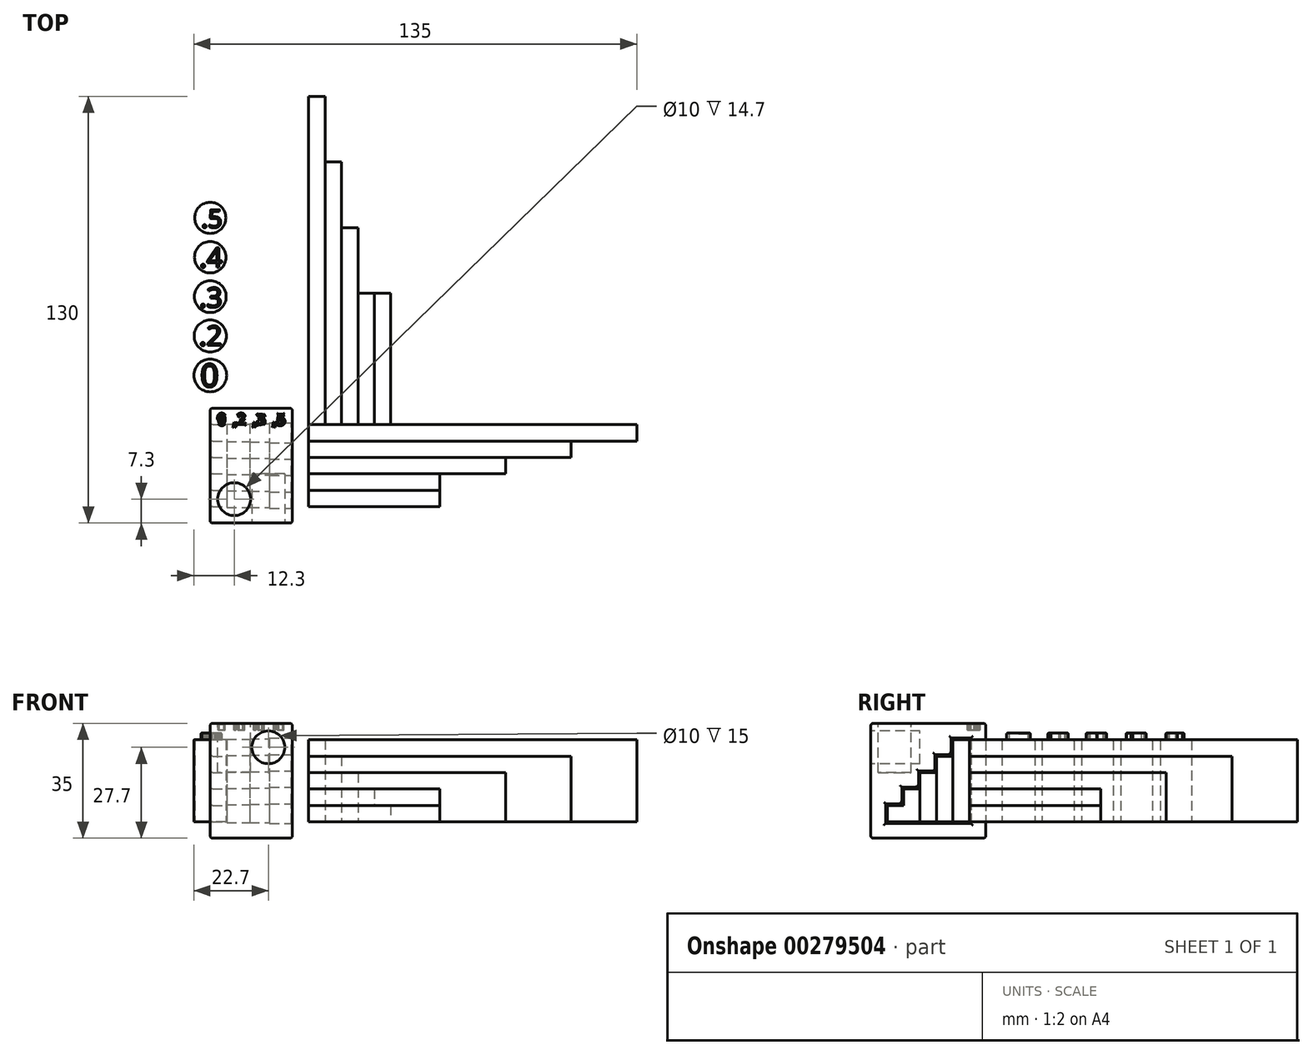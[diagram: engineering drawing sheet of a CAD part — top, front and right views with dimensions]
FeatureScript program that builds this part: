
annotation { "Feature Type Name" : "Feature", "Feature Type Description" : "" }
export const myFeature = defineFeature(function(context is Context, id is Id, definition is map)
    precondition{}
    {
        {
            var Q0;
            Q0=qCreatedBy(makeId("Top.planeOp"),FACE);
            var sketch = newSketch(context, id + "F0", { "sketchPlane" : qUnion([Q0])});
            skLineSegment(sketch, "E0.bottom", {"start": v(0, 0) * mm, "end": v(5, 0) * mm});
            skLineSegment(sketch, "E0.top", {"start": v(0, 100) * mm, "end": v(5, 100) * mm});
            skLineSegment(sketch, "E0.left", {"start": v(0, 0) * mm, "end": v(0, 100) * mm});
            skLineSegment(sketch, "E0.right", {"start": v(5, 0) * mm, "end": v(5, 100) * mm});
            skLineSegment(sketch, "E1.bottom", {"start": v(5, 0) * mm, "end": v(10, 0) * mm});
            skLineSegment(sketch, "E1.top", {"start": v(5, 80) * mm, "end": v(10, 80) * mm});
            skLineSegment(sketch, "E1.left", {"start": v(5, 0) * mm, "end": v(5, 80) * mm});
            skLineSegment(sketch, "E1.right", {"start": v(10, 0) * mm, "end": v(10, 80) * mm});
            skLineSegment(sketch, "E2.bottom", {"start": v(10, 0) * mm, "end": v(15, 0) * mm});
            skLineSegment(sketch, "E2.top", {"start": v(10, 60) * mm, "end": v(15, 60) * mm});
            skLineSegment(sketch, "E2.left", {"start": v(10, 0) * mm, "end": v(10, 60) * mm});
            skLineSegment(sketch, "E2.right", {"start": v(15, 0) * mm, "end": v(15, 60) * mm});
            skLineSegment(sketch, "E3.bottom", {"start": v(15, 0) * mm, "end": v(20, 0) * mm});
            skLineSegment(sketch, "E3.top", {"start": v(15, 40) * mm, "end": v(20, 40) * mm});
            skLineSegment(sketch, "E3.left", {"start": v(15, 0) * mm, "end": v(15, 40) * mm});
            skLineSegment(sketch, "E3.right", {"start": v(20, 0) * mm, "end": v(20, 40) * mm});
            skLineSegment(sketch, "E4.bottom", {"start": v(20, 0) * mm, "end": v(25, 0) * mm});
            skLineSegment(sketch, "E4.top", {"start": v(20, 40) * mm, "end": v(25, 40) * mm});
            skLineSegment(sketch, "E4.right", {"start": v(25, 0) * mm, "end": v(25, 40) * mm});
            skLineSegment(sketch, "E5.bottom", {"start": v(-5, -30) * mm, "end": v(-30, -30) * mm});
            skLineSegment(sketch, "E5.top", {"start": v(-5, 5) * mm, "end": v(-30, 5) * mm});
            skLineSegment(sketch, "E5.left", {"start": v(-5, -30) * mm, "end": v(-5, 5) * mm});
            skLineSegment(sketch, "E5.right", {"start": v(-30, -30) * mm, "end": v(-30, 5) * mm});
            skCircle(sketch, "E6", {"center": v(-30, 15) * mm, "radius": 5 * mm});
            skCircle(sketch, "E7", {"center": v(-30, 27) * mm, "radius": 4.9 * mm});
            skCircle(sketch, "E8", {"center": v(-30, 39) * mm, "radius": 4.85 * mm});
            skCircle(sketch, "E9", {"center": v(-30, 51) * mm, "radius": 4.8 * mm});
            skCircle(sketch, "E10", {"center": v(-30, 63) * mm, "radius": 4.75 * mm});
            skSolve(sketch);
        }
        {
            var Q0;
            Q0=makeQuery(id+"F0.imprint","IMPRINT",FACE,{"disambiguationData":[TD([[makeQuery(id+"F0.imprint","IMPRINT",EDGE,{"derivedFrom":sQuery(id+"F0.wireOp",EDGE,"E0.bottom")}),1.0]])]});
            extrude(context, id + "F1", {"entities" : qUnion([Q0]), "depth" : 25 * mm, "offsetDistance" : 25 * mm});
        }
        {
            var Q0;
            Q0=makeQuery(id+"F0.imprint","IMPRINT",FACE,{"disambiguationData":[TD([[makeQuery(id+"F0.imprint","IMPRINT",EDGE,{"derivedFrom":sQuery(id+"F0.wireOp",EDGE,"E1.bottom")}),1.0]])]});
            extrude(context, id + "F2", {"entities" : qUnion([Q0]), "operationType" : NewBodyOperationType.ADD, "depth" : 20 * mm, "offsetDistance" : 25 * mm});
        }
        {
            var Q0;
            Q0=makeQuery(id+"F0.imprint","IMPRINT",FACE,{"disambiguationData":[TD([[makeQuery(id+"F0.imprint","IMPRINT",EDGE,{"derivedFrom":sQuery(id+"F0.wireOp",EDGE,"E2.bottom")}),1.0]])]});
            extrude(context, id + "F3", {"entities" : qUnion([Q0]), "operationType" : NewBodyOperationType.ADD, "depth" : 15 * mm, "offsetDistance" : 25 * mm});
        }
        {
            var Q0;
            Q0=makeQuery(id+"F0.imprint","IMPRINT",FACE,{"disambiguationData":[TD([[makeQuery(id+"F0.imprint","IMPRINT",EDGE,{"derivedFrom":sQuery(id+"F0.wireOp",EDGE,"E3.bottom")}),1.0]])]});
            extrude(context, id + "F4", {"entities" : qUnion([Q0]), "operationType" : NewBodyOperationType.ADD, "depth" : 10 * mm, "offsetDistance" : 25 * mm});
        }
        {
            var Q0;
            Q0=makeQuery(id+"F0.imprint","IMPRINT",FACE,{"disambiguationData":[TD([[makeQuery(id+"F0.imprint","IMPRINT",EDGE,{"derivedFrom":sQuery(id+"F0.wireOp",EDGE,"E4.bottom")}),1.0]])]});
            extrude(context, id + "F5", {"entities" : qUnion([Q0]), "operationType" : NewBodyOperationType.ADD, "depth" : 5 * mm, "offsetDistance" : 25 * mm});
        }
        {
            var Q0;
            Q0=makeQuery(id+"F1.opExtrude","SWEPT_BODY",BODY,{"disambiguationData":[OSD([sQuery(id+"F0.wireOp",EDGE,"E0.bottom"),sQuery(id+"F0.wireOp",EDGE,"E0.top"),sQuery(id+"F0.wireOp",EDGE,"E0.left"),sQuery(id+"F0.wireOp",EDGE,"E0.right"),sQuery(id+"F0.wireOp",EDGE,"E1.left")])]});
            var Q1;
            Q1=makeQuery(id+"F1.opExtrude","SWEPT_EDGE",EDGE,{"disambiguationData":[OSD([sQuery(id+"F0.wireOp",EDGE,"E0.bottom"),sQuery(id+"F0.wireOp",EDGE,"E0.left")])]});
            circularPattern(context, id + "F6", {"entities" : qUnion([Q0]), "axis" : qUnion([Q1]), "angle" : 90 * degree, "instanceCount" : 2, "equalSpace" : true});
        }
        {
            var Q0;
            Q0=makeQuery(id+"F0.imprint","IMPRINT",FACE,{"disambiguationData":[TD([[makeQuery(id+"F0.imprint","IMPRINT",EDGE,{"derivedFrom":sQuery(id+"F0.wireOp",EDGE,"E5.bottom")}),-1.0]])]});
            extrude(context, id + "F7", {"entities" : qUnion([Q0]), "depth" : 30 * mm, "offsetDistance" : 25 * mm, "hasSecondDirection" : true, "secondDirectionOppositeDirection" : true, "secondDirectionDepth" : 5 * mm});
        }
        {
            var Q0;
            Q0=makeQuery(id+"F6.opPattern","COPY",FACE,{"derivedFrom":makeQuery(id+"F5.boolean.opBoolean","MERGE",FACE,{"derivedFrom":[makeQuery(id+"F4.boolean.opBoolean","MERGE",FACE,{"derivedFrom":[makeQuery(id+"F3.boolean.opBoolean","MERGE",FACE,{"derivedFrom":[makeQuery(id+"F2.boolean.opBoolean","MERGE",FACE,{"derivedFrom":[makeQuery(id+"F1.opExtrude","SWEPT_FACE",FACE,{"disambiguationData":[OSD([sQuery(id+"F0.wireOp",EDGE,"E0.bottom")])]}),makeQuery(id+"F2.opExtrude","SWEPT_FACE",FACE,{"disambiguationData":[OSD([sQuery(id+"F0.wireOp",EDGE,"E1.bottom")])]})]}),makeQuery(id+"F3.opExtrude","SWEPT_FACE",FACE,{"disambiguationData":[OSD([sQuery(id+"F0.wireOp",EDGE,"E2.bottom")])]})]}),makeQuery(id+"F4.opExtrude","SWEPT_FACE",FACE,{"disambiguationData":[OSD([sQuery(id+"F0.wireOp",EDGE,"E3.bottom")])]})]}),makeQuery(id+"F5.opExtrude","SWEPT_FACE",FACE,{"disambiguationData":[OSD([sQuery(id+"F0.wireOp",EDGE,"E4.bottom")])]})]}),"instanceName":"1"});
            var sketch = newSketch(context, id + "F8", { "sketchPlane" : qUnion([Q0])});
            skLineSegment(sketch, "E11.0", {"start": v(-0.2, 25.2) * mm, "end": v(-0.2, -0.2) * mm});
            skLineSegment(sketch, "E11.1", {"start": v(15.2, 10.2) * mm, "end": v(20.2, 10.2) * mm});
            skLineSegment(sketch, "E11.2", {"start": v(20.2, 10.2) * mm, "end": v(20.2, 5.2) * mm});
            skLineSegment(sketch, "E11.3", {"start": v(20.2, 5.2) * mm, "end": v(25.2, 5.2) * mm});
            skLineSegment(sketch, "E11.4", {"start": v(25.2, 5.2) * mm, "end": v(25.2, -0.2) * mm});
            skLineSegment(sketch, "E11.5", {"start": v(15.2, 15.2) * mm, "end": v(15.2, 10.2) * mm});
            skLineSegment(sketch, "E11.6", {"start": v(-0.2, -0.2) * mm, "end": v(25.2, -0.2) * mm});
            skLineSegment(sketch, "E11.7", {"start": v(10.2, 15.2) * mm, "end": v(15.2, 15.2) * mm});
            skLineSegment(sketch, "E11.8", {"start": v(10.2, 20.2) * mm, "end": v(10.2, 15.2) * mm});
            skLineSegment(sketch, "E11.9", {"start": v(5.2, 20.2) * mm, "end": v(10.2, 20.2) * mm});
            skLineSegment(sketch, "E11.10", {"start": v(5.2, 25.2) * mm, "end": v(5.2, 20.2) * mm});
            skLineSegment(sketch, "E11.11", {"start": v(-0.2, 25.2) * mm, "end": v(5.2, 25.2) * mm});
            skLineSegment(sketch, "E12.0", {"start": v(-0.3, 25.3) * mm, "end": v(5.3, 25.3) * mm});
            skLineSegment(sketch, "E12.1", {"start": v(20.3, 10.3) * mm, "end": v(20.3, 5.3) * mm});
            skLineSegment(sketch, "E12.2", {"start": v(20.3, 5.3) * mm, "end": v(25.3, 5.3) * mm});
            skLineSegment(sketch, "E12.3", {"start": v(25.3, 5.3) * mm, "end": v(25.3, -0.3) * mm});
            skLineSegment(sketch, "E12.4", {"start": v(-0.3, -0.3) * mm, "end": v(25.3, -0.3) * mm});
            skLineSegment(sketch, "E12.5", {"start": v(15.3, 10.3) * mm, "end": v(20.3, 10.3) * mm});
            skLineSegment(sketch, "E12.6", {"start": v(-0.3, 25.3) * mm, "end": v(-0.3, -0.3) * mm});
            skLineSegment(sketch, "E12.7", {"start": v(15.3, 15.3) * mm, "end": v(15.3, 10.3) * mm});
            skLineSegment(sketch, "E12.8", {"start": v(10.3, 15.3) * mm, "end": v(15.3, 15.3) * mm});
            skLineSegment(sketch, "E12.9", {"start": v(10.3, 20.3) * mm, "end": v(10.3, 15.3) * mm});
            skLineSegment(sketch, "E12.10", {"start": v(5.3, 20.3) * mm, "end": v(10.3, 20.3) * mm});
            skLineSegment(sketch, "E12.11", {"start": v(5.3, 25.3) * mm, "end": v(5.3, 20.3) * mm});
            skLineSegment(sketch, "E13.0", {"start": v(-0.5, 25.5) * mm, "end": v(5.5, 25.5) * mm});
            skLineSegment(sketch, "E13.1", {"start": v(20.5, 10.5) * mm, "end": v(20.5, 5.5) * mm});
            skLineSegment(sketch, "E13.2", {"start": v(20.5, 5.5) * mm, "end": v(25.5, 5.5) * mm});
            skLineSegment(sketch, "E13.3", {"start": v(25.5, 5.5) * mm, "end": v(25.5, -0.5) * mm});
            skLineSegment(sketch, "E13.4", {"start": v(-0.5, -0.5) * mm, "end": v(25.5, -0.5) * mm});
            skLineSegment(sketch, "E13.5", {"start": v(15.5, 10.5) * mm, "end": v(20.5, 10.5) * mm});
            skLineSegment(sketch, "E13.6", {"start": v(-0.5, 25.5) * mm, "end": v(-0.5, -0.5) * mm});
            skLineSegment(sketch, "E13.7", {"start": v(15.5, 15.5) * mm, "end": v(15.5, 10.5) * mm});
            skLineSegment(sketch, "E13.8", {"start": v(10.5, 15.5) * mm, "end": v(15.5, 15.5) * mm});
            skLineSegment(sketch, "E13.9", {"start": v(10.5, 20.5) * mm, "end": v(10.5, 15.5) * mm});
            skLineSegment(sketch, "E13.10", {"start": v(5.5, 20.5) * mm, "end": v(10.5, 20.5) * mm});
            skLineSegment(sketch, "E13.11", {"start": v(5.5, 25.5) * mm, "end": v(5.5, 20.5) * mm});
            skSolve(sketch);
        }
        {
            var Q0;
            {var subQ4=sQuery(id+"F0.wireOp",EDGE,"E0.bottom");Q0=makeQuery(id+"F8.imprint","IMPRINT",FACE,{"disambiguationData":[TD([[makeQuery(id+"F8.imprint","IMPRINT",EDGE,{"derivedFrom":makeQuery(id+"F6.opPattern","COPY",EDGE,{"derivedFrom":makeQuery(id+"F1.opExtrude","CAP_EDGE",EDGE,{"disambiguationData":[OSD([subQ4])],"isStart":false}),"instanceName":"1"})}),-1.0]])]});}
            var Q1;
            Q1=makeQuery(id+"F7.opExtrude","SWEPT_FACE",FACE,{"disambiguationData":[OSD([sQuery(id+"F0.wireOp",EDGE,"E5.right")])]});
            extrude(context, id + "F9", {"entities" : qUnion([Q0]), "operationType" : NewBodyOperationType.REMOVE, "endBound" : BoundingType.UP_TO_SURFACE, "depth" : 25 * mm, "endBoundEntityFace" : qUnion([Q1]), "offsetDistance" : 25 * mm});
        }
        {
            var Q0;
            Q0=makeQuery(id+"F8.imprint","IMPRINT",FACE,{"disambiguationData":[TD([[makeQuery(id+"F8.imprint","IMPRINT",EDGE,{"derivedFrom":sQuery(id+"F8.wireOp",EDGE,"E11.0")}),1.0]])]});
            extrude(context, id + "F10", {"entities" : qUnion([Q0]), "operationType" : NewBodyOperationType.REMOVE, "depth" : 25 * mm, "offsetDistance" : 25 * mm});
        }
        {
            var Q0;
            Q0=makeQuery(id+"F8.imprint","IMPRINT",FACE,{"disambiguationData":[TD([[makeQuery(id+"F8.imprint","IMPRINT",EDGE,{"derivedFrom":sQuery(id+"F8.wireOp",EDGE,"E11.0")}),-1.0]])]});
            extrude(context, id + "F11", {"entities" : qUnion([Q0]), "operationType" : NewBodyOperationType.REMOVE, "depth" : 18 * mm, "offsetDistance" : 25 * mm});
        }
        {
            var Q0;
            Q0=makeQuery(id+"F7.opExtrude","SWEPT_FACE",FACE,{"disambiguationData":[OSD([sQuery(id+"F0.wireOp",EDGE,"E5.left")])]});
            var Q1;
            Q1=makeQuery(id+"F7.opExtrude","SWEPT_FACE",FACE,{"disambiguationData":[OSD([sQuery(id+"F0.wireOp",EDGE,"E5.right")])]});
            var Q2;
            Q2=makeQuery(id+"F7.opExtrude","CAP_EDGE",EDGE,{"disambiguationData":[OSD([sQuery(id+"F0.wireOp",EDGE,"E5.bottom")])],"isStart":false});
            var Q3;
            Q3=makeQuery(id+"F7.opExtrude","CAP_EDGE",EDGE,{"disambiguationData":[OSD([sQuery(id+"F0.wireOp",EDGE,"E5.top")])],"isStart":false});
            var Q4;
            Q4=makeQuery(id+"F7.opExtrude","CAP_EDGE",EDGE,{"disambiguationData":[OSD([sQuery(id+"F0.wireOp",EDGE,"E5.bottom")])],"isStart":true});
            var Q5;
            Q5=makeQuery(id+"F7.opExtrude","CAP_EDGE",EDGE,{"disambiguationData":[OSD([sQuery(id+"F0.wireOp",EDGE,"E5.top")])],"isStart":true});
            fillet(context, id + "F12", {"entities" : qUnion([Q0, Q1, Q2, Q3, Q4, Q5]), "radius" : 0.7 * mm, "tangentPropagation" : true, "allowEdgeOverflow" : false});
        }
        {
            var Q0;
            Q0=makeQuery(id+"F8.imprint","IMPRINT",FACE,{"disambiguationData":[TD([[makeQuery(id+"F8.imprint","IMPRINT",EDGE,{"derivedFrom":sQuery(id+"F8.wireOp",EDGE,"E12.0")}),1.0]])]});
            extrude(context, id + "F13", {"entities" : qUnion([Q0]), "operationType" : NewBodyOperationType.REMOVE, "depth" : 12 * mm, "offsetDistance" : 25 * mm});
        }
        {
            var Q0;
            Q0=makeQuery(id+"F7.opExtrude","CAP_FACE",FACE,{"disambiguationData":[OSD([sQuery(id+"F0.wireOp",EDGE,"E5.bottom"),sQuery(id+"F0.wireOp",EDGE,"E5.top"),sQuery(id+"F0.wireOp",EDGE,"E5.left"),sQuery(id+"F0.wireOp",EDGE,"E5.right")])],"isStart":false});
            var sketch = newSketch(context, id + "F14", { "sketchPlane" : qUnion([Q0])});
            skCircle(sketch, "E14", {"center": v(-22.7, -22.7) * mm, "radius": 5 * mm});
            skText(sketch, "E15", { "text": "0  ,2  ,3  ,5", "fontName": "OpenSans-Regular.ttf"});
            const initialGuessF14  = {"E15": [-0.0278, 0, 1, 0, 0.00323]};
            skSetInitialGuess(sketch, initialGuessF14);
            skSolve(sketch);
        }
        {
            var Q0;
            Q0=makeQuery(id+"F14.imprint","IMPRINT",FACE,{"disambiguationData":[TD([[makeQuery(id+"F14.imprint","IMPRINT",EDGE,{"derivedFrom":sQuery(id+"F14.wireOp",EDGE,"E14")}),1.0]])]});
            extrude(context, id + "F15", {"entities" : qUnion([Q0]), "operationType" : NewBodyOperationType.REMOVE, "oppositeDirection" : true, "depth" : 15 * mm, "offsetDistance" : 25 * mm});
        }
        {
            var Q0;
            Q0=makeQuery(id+"F7.opExtrude","SWEPT_FACE",FACE,{"disambiguationData":[OSD([sQuery(id+"F0.wireOp",EDGE,"E5.bottom")])]});
            var sketch = newSketch(context, id + "F16", { "sketchPlane" : qUnion([Q0])});
            skCircle(sketch, "E16", {"center": v(-12.3, 22.7) * mm, "radius": 5 * mm});
            skSolve(sketch);
        }
        {
            var Q0;
            Q0=makeQuery(id+"F16.imprint","IMPRINT",FACE,{"disambiguationData":[TD([[makeQuery(id+"F16.imprint","IMPRINT",EDGE,{"derivedFrom":sQuery(id+"F16.wireOp",EDGE,"E16")}),1.0]])]});
            extrude(context, id + "F17", {"entities" : qUnion([Q0]), "operationType" : NewBodyOperationType.REMOVE, "oppositeDirection" : true, "depth" : 15 * mm, "offsetDistance" : 25 * mm});
        }
        {
            var Q0;
            Q0=makeQuery(id+"F0.imprint","IMPRINT",FACE,{"disambiguationData":[TD([[makeQuery(id+"F0.imprint","IMPRINT",EDGE,{"derivedFrom":sQuery(id+"F0.wireOp",EDGE,"E6")}),1.0]])]});
            var Q1;
            Q1=makeQuery(id+"F0.imprint","IMPRINT",FACE,{"disambiguationData":[TD([[makeQuery(id+"F0.imprint","IMPRINT",EDGE,{"derivedFrom":sQuery(id+"F0.wireOp",EDGE,"E7")}),1.0]])]});
            var Q2;
            Q2=makeQuery(id+"F0.imprint","IMPRINT",FACE,{"disambiguationData":[TD([[makeQuery(id+"F0.imprint","IMPRINT",EDGE,{"derivedFrom":sQuery(id+"F0.wireOp",EDGE,"E8")}),1.0]])]});
            var Q3;
            Q3=makeQuery(id+"F0.imprint","IMPRINT",FACE,{"disambiguationData":[TD([[makeQuery(id+"F0.imprint","IMPRINT",EDGE,{"derivedFrom":sQuery(id+"F0.wireOp",EDGE,"E9")}),1.0]])]});
            var Q4;
            Q4=makeQuery(id+"F0.imprint","IMPRINT",FACE,{"disambiguationData":[TD([[makeQuery(id+"F0.imprint","IMPRINT",EDGE,{"derivedFrom":sQuery(id+"F0.wireOp",EDGE,"E10")}),1.0]])]});
            extrude(context, id + "F18", {"entities" : qUnion([Q0, Q1, Q2, Q3, Q4]), "depth" : 25 * mm, "offsetDistance" : 25 * mm});
        }
        {
            var Q0;
            Q0=makeQuery(id+"F18.opExtrude","CAP_FACE",FACE,{"disambiguationData":[OSD([sQuery(id+"F0.wireOp",EDGE,"E10")])],"isStart":false});
            var sketch = newSketch(context, id + "F19", { "sketchPlane" : qUnion([Q0])});
            skText(sketch, "E17", { "text": ".5", "fontName": "OpenSans-Regular.ttf"});
            skText(sketch, "E18", { "text": ".4", "fontName": "OpenSans-Regular.ttf"});
            skText(sketch, "E19", { "text": ".3", "fontName": "OpenSans-Regular.ttf"});
            skText(sketch, "E20", { "text": ".2", "fontName": "OpenSans-Regular.ttf"});
            skText(sketch, "E21", { "text": "0", "fontName": "OpenSans-Regular.ttf"});
            skPoint(sketch, "E21.firstSnap0", {"position": v(-33, 26.47) * mm});
            const initialGuessF19  = {"E17": [-0.03275, 0.06003, 1, 0, 0.0055], "E18": [-0.0333, 0.0479, 1, 0, 0.006], "E19": [-0.03335, 0.03575, 1, 0, 0.006], "E20": [-0.0334, 0.0241, 1, 0, 0.006], "E21": [-0.033, 0.0115, 1, 0, 0.007]};
            skSetInitialGuess(sketch, initialGuessF19);
            skSolve(sketch);
        }
        {
            var Q0;
            Q0=makeQuery(id+"F19.imprint","IMPRINT",FACE,{"disambiguationData":[TD([[makeQuery(id+"F19.imprint","IMPRINT",EDGE,{"derivedFrom":sQuery(id+"F19.wireOp",EDGE,"E17.sketch_text.stroke-8")}),-1.0]])]});
            var Q1;
            Q1=makeQuery(id+"F19.imprint","IMPRINT",FACE,{"disambiguationData":[TD([[makeQuery(id+"F19.imprint","IMPRINT",EDGE,{"derivedFrom":sQuery(id+"F19.wireOp",EDGE,"E17.sketch_text.stroke-0")}),-1.0]])]});
            var Q2;
            Q2=makeQuery(id+"F19.imprint","IMPRINT",FACE,{"disambiguationData":[TD([[makeQuery(id+"F19.imprint","IMPRINT",EDGE,{"derivedFrom":sQuery(id+"F19.wireOp",EDGE,"E18.sketch_text.stroke-8")}),-1.0]])]});
            var Q3;
            Q3=makeQuery(id+"F19.imprint","IMPRINT",FACE,{"disambiguationData":[TD([[makeQuery(id+"F19.imprint","IMPRINT",EDGE,{"derivedFrom":sQuery(id+"F19.wireOp",EDGE,"E18.sketch_text.stroke-0")}),-1.0]])]});
            var Q4;
            Q4=makeQuery(id+"F19.imprint","IMPRINT",FACE,{"disambiguationData":[TD([[makeQuery(id+"F19.imprint","IMPRINT",EDGE,{"derivedFrom":sQuery(id+"F19.wireOp",EDGE,"E19.sketch_text.stroke-8")}),-1.0]])]});
            var Q5;
            Q5=makeQuery(id+"F19.imprint","IMPRINT",FACE,{"disambiguationData":[TD([[makeQuery(id+"F19.imprint","IMPRINT",EDGE,{"derivedFrom":sQuery(id+"F19.wireOp",EDGE,"E19.sketch_text.stroke-0")}),-1.0]])]});
            var Q6;
            Q6=makeQuery(id+"F19.imprint","IMPRINT",FACE,{"disambiguationData":[TD([[makeQuery(id+"F19.imprint","IMPRINT",EDGE,{"derivedFrom":sQuery(id+"F19.wireOp",EDGE,"E20.sketch_text.stroke-8")}),-1.0]])]});
            var Q7;
            Q7=makeQuery(id+"F19.imprint","IMPRINT",FACE,{"disambiguationData":[TD([[makeQuery(id+"F19.imprint","IMPRINT",EDGE,{"derivedFrom":sQuery(id+"F19.wireOp",EDGE,"E20.sketch_text.stroke-0")}),-1.0]])]});
            var Q8;
            Q8=makeQuery(id+"F19.imprint","IMPRINT",FACE,{"disambiguationData":[TD([[makeQuery(id+"F19.imprint","IMPRINT",EDGE,{"derivedFrom":sQuery(id+"F19.wireOp",EDGE,"E21.sketch_text.stroke-0")}),-1.0]])]});
            extrude(context, id + "F20", {"entities" : qUnion([Q0, Q1, Q2, Q3, Q4, Q5, Q6, Q7, Q8]), "depth" : 2 * mm, "offsetDistance" : 25 * mm});
        }
        {
            var Q0;
            Q0=makeQuery(id+"F18.opExtrude","CAP_EDGE",EDGE,{"disambiguationData":[OSD([sQuery(id+"F0.wireOp",EDGE,"E10")])],"isStart":false});
            var Q1;
            Q1=makeQuery(id+"F18.opExtrude","CAP_EDGE",EDGE,{"disambiguationData":[OSD([sQuery(id+"F0.wireOp",EDGE,"E9")])],"isStart":false});
            var Q2;
            Q2=makeQuery(id+"F18.opExtrude","CAP_EDGE",EDGE,{"disambiguationData":[OSD([sQuery(id+"F0.wireOp",EDGE,"E8")])],"isStart":false});
            var Q3;
            Q3=makeQuery(id+"F18.opExtrude","CAP_EDGE",EDGE,{"disambiguationData":[OSD([sQuery(id+"F0.wireOp",EDGE,"E7")])],"isStart":false});
            var Q4;
            Q4=makeQuery(id+"F18.opExtrude","CAP_EDGE",EDGE,{"disambiguationData":[OSD([sQuery(id+"F0.wireOp",EDGE,"E6")])],"isStart":false});
            var Q5;
            Q5=makeQuery(id+"F20.opExtrude","CAP_FACE",FACE,{"disambiguationData":[OSD([sQuery(id+"F19.wireOp",EDGE,"E20.sketch_text.stroke-0"),sQuery(id+"F19.wireOp",EDGE,"E20.sketch_text.stroke-1"),sQuery(id+"F19.wireOp",EDGE,"E20.sketch_text.stroke-2"),sQuery(id+"F19.wireOp",EDGE,"E20.sketch_text.stroke-3"),sQuery(id+"F19.wireOp",EDGE,"E20.sketch_text.stroke-4"),sQuery(id+"F19.wireOp",EDGE,"E20.sketch_text.stroke-5"),sQuery(id+"F19.wireOp",EDGE,"E20.sketch_text.stroke-6"),sQuery(id+"F19.wireOp",EDGE,"E20.sketch_text.stroke-7")])],"isStart":false});
            var Q6;
            Q6=makeQuery(id+"F20.opExtrude","CAP_FACE",FACE,{"disambiguationData":[OSD([sQuery(id+"F19.wireOp",EDGE,"E19.sketch_text.stroke-0"),sQuery(id+"F19.wireOp",EDGE,"E19.sketch_text.stroke-1"),sQuery(id+"F19.wireOp",EDGE,"E19.sketch_text.stroke-2"),sQuery(id+"F19.wireOp",EDGE,"E19.sketch_text.stroke-3"),sQuery(id+"F19.wireOp",EDGE,"E19.sketch_text.stroke-4"),sQuery(id+"F19.wireOp",EDGE,"E19.sketch_text.stroke-5"),sQuery(id+"F19.wireOp",EDGE,"E19.sketch_text.stroke-6"),sQuery(id+"F19.wireOp",EDGE,"E19.sketch_text.stroke-7")])],"isStart":false});
            var Q7;
            Q7=makeQuery(id+"F20.opExtrude","CAP_FACE",FACE,{"disambiguationData":[OSD([sQuery(id+"F19.wireOp",EDGE,"E21.sketch_text.stroke-0"),sQuery(id+"F19.wireOp",EDGE,"E21.sketch_text.stroke-1"),sQuery(id+"F19.wireOp",EDGE,"E21.sketch_text.stroke-2"),sQuery(id+"F19.wireOp",EDGE,"E21.sketch_text.stroke-3"),sQuery(id+"F19.wireOp",EDGE,"E21.sketch_text.stroke-4"),sQuery(id+"F19.wireOp",EDGE,"E21.sketch_text.stroke-5"),sQuery(id+"F19.wireOp",EDGE,"E21.sketch_text.stroke-6"),sQuery(id+"F19.wireOp",EDGE,"E21.sketch_text.stroke-7"),sQuery(id+"F19.wireOp",EDGE,"E21.sketch_text.stroke-8"),sQuery(id+"F19.wireOp",EDGE,"E21.sketch_text.stroke-9"),sQuery(id+"F19.wireOp",EDGE,"E21.sketch_text.stroke-10"),sQuery(id+"F19.wireOp",EDGE,"E21.sketch_text.stroke-11"),sQuery(id+"F19.wireOp",EDGE,"E21.sketch_text.stroke-12"),sQuery(id+"F19.wireOp",EDGE,"E21.sketch_text.stroke-13"),sQuery(id+"F19.wireOp",EDGE,"E21.sketch_text.stroke-14"),sQuery(id+"F19.wireOp",EDGE,"E21.sketch_text.stroke-15")])],"isStart":false});
            var Q8;
            Q8=makeQuery(id+"F20.opExtrude","CAP_FACE",FACE,{"disambiguationData":[OSD([sQuery(id+"F19.wireOp",EDGE,"E20.sketch_text.stroke-8"),sQuery(id+"F19.wireOp",EDGE,"E20.sketch_text.stroke-9"),sQuery(id+"F19.wireOp",EDGE,"E20.sketch_text.stroke-10"),sQuery(id+"F19.wireOp",EDGE,"E20.sketch_text.stroke-11"),sQuery(id+"F19.wireOp",EDGE,"E20.sketch_text.stroke-12"),sQuery(id+"F19.wireOp",EDGE,"E20.sketch_text.stroke-13"),sQuery(id+"F19.wireOp",EDGE,"E20.sketch_text.stroke-14"),sQuery(id+"F19.wireOp",EDGE,"E20.sketch_text.stroke-15"),sQuery(id+"F19.wireOp",EDGE,"E20.sketch_text.stroke-16"),sQuery(id+"F19.wireOp",EDGE,"E20.sketch_text.stroke-17"),sQuery(id+"F19.wireOp",EDGE,"E20.sketch_text.stroke-18"),sQuery(id+"F19.wireOp",EDGE,"E20.sketch_text.stroke-19"),sQuery(id+"F19.wireOp",EDGE,"E20.sketch_text.stroke-20"),sQuery(id+"F19.wireOp",EDGE,"E20.sketch_text.stroke-21"),sQuery(id+"F19.wireOp",EDGE,"E20.sketch_text.stroke-22"),sQuery(id+"F19.wireOp",EDGE,"E20.sketch_text.stroke-23"),sQuery(id+"F19.wireOp",EDGE,"E20.sketch_text.stroke-24"),sQuery(id+"F19.wireOp",EDGE,"E20.sketch_text.stroke-25"),sQuery(id+"F19.wireOp",EDGE,"E20.sketch_text.stroke-26"),sQuery(id+"F19.wireOp",EDGE,"E20.sketch_text.stroke-27")])],"isStart":false});
            var Q9;
            Q9=makeQuery(id+"F20.opExtrude","CAP_FACE",FACE,{"disambiguationData":[OSD([sQuery(id+"F19.wireOp",EDGE,"E19.sketch_text.stroke-8"),sQuery(id+"F19.wireOp",EDGE,"E19.sketch_text.stroke-9"),sQuery(id+"F19.wireOp",EDGE,"E19.sketch_text.stroke-10"),sQuery(id+"F19.wireOp",EDGE,"E19.sketch_text.stroke-11"),sQuery(id+"F19.wireOp",EDGE,"E19.sketch_text.stroke-12"),sQuery(id+"F19.wireOp",EDGE,"E19.sketch_text.stroke-13"),sQuery(id+"F19.wireOp",EDGE,"E19.sketch_text.stroke-14"),sQuery(id+"F19.wireOp",EDGE,"E19.sketch_text.stroke-15"),sQuery(id+"F19.wireOp",EDGE,"E19.sketch_text.stroke-16"),sQuery(id+"F19.wireOp",EDGE,"E19.sketch_text.stroke-17"),sQuery(id+"F19.wireOp",EDGE,"E19.sketch_text.stroke-18"),sQuery(id+"F19.wireOp",EDGE,"E19.sketch_text.stroke-19"),sQuery(id+"F19.wireOp",EDGE,"E19.sketch_text.stroke-20"),sQuery(id+"F19.wireOp",EDGE,"E19.sketch_text.stroke-21"),sQuery(id+"F19.wireOp",EDGE,"E19.sketch_text.stroke-22"),sQuery(id+"F19.wireOp",EDGE,"E19.sketch_text.stroke-23"),sQuery(id+"F19.wireOp",EDGE,"E19.sketch_text.stroke-24"),sQuery(id+"F19.wireOp",EDGE,"E19.sketch_text.stroke-25"),sQuery(id+"F19.wireOp",EDGE,"E19.sketch_text.stroke-26"),sQuery(id+"F19.wireOp",EDGE,"E19.sketch_text.stroke-27"),sQuery(id+"F19.wireOp",EDGE,"E19.sketch_text.stroke-28"),sQuery(id+"F19.wireOp",EDGE,"E19.sketch_text.stroke-29"),sQuery(id+"F19.wireOp",EDGE,"E19.sketch_text.stroke-30"),sQuery(id+"F19.wireOp",EDGE,"E19.sketch_text.stroke-31"),sQuery(id+"F19.wireOp",EDGE,"E19.sketch_text.stroke-32"),sQuery(id+"F19.wireOp",EDGE,"E19.sketch_text.stroke-33"),sQuery(id+"F19.wireOp",EDGE,"E19.sketch_text.stroke-34"),sQuery(id+"F19.wireOp",EDGE,"E19.sketch_text.stroke-35")])],"isStart":false});
            var Q10;
            Q10=makeQuery(id+"F20.opExtrude","CAP_FACE",FACE,{"disambiguationData":[OSD([sQuery(id+"F19.wireOp",EDGE,"E18.sketch_text.stroke-8"),sQuery(id+"F19.wireOp",EDGE,"E18.sketch_text.stroke-9"),sQuery(id+"F19.wireOp",EDGE,"E18.sketch_text.stroke-10"),sQuery(id+"F19.wireOp",EDGE,"E18.sketch_text.stroke-11"),sQuery(id+"F19.wireOp",EDGE,"E18.sketch_text.stroke-12"),sQuery(id+"F19.wireOp",EDGE,"E18.sketch_text.stroke-13"),sQuery(id+"F19.wireOp",EDGE,"E18.sketch_text.stroke-14"),sQuery(id+"F19.wireOp",EDGE,"E18.sketch_text.stroke-15"),sQuery(id+"F19.wireOp",EDGE,"E18.sketch_text.stroke-16"),sQuery(id+"F19.wireOp",EDGE,"E18.sketch_text.stroke-17"),sQuery(id+"F19.wireOp",EDGE,"E18.sketch_text.stroke-18"),sQuery(id+"F19.wireOp",EDGE,"E18.sketch_text.stroke-19"),sQuery(id+"F19.wireOp",EDGE,"E18.sketch_text.stroke-20"),sQuery(id+"F19.wireOp",EDGE,"E18.sketch_text.stroke-21"),sQuery(id+"F19.wireOp",EDGE,"E18.sketch_text.stroke-22"),sQuery(id+"F19.wireOp",EDGE,"E18.sketch_text.stroke-23"),sQuery(id+"F19.wireOp",EDGE,"E18.sketch_text.stroke-24")])],"isStart":false});
            var Q11;
            Q11=makeQuery(id+"F20.opExtrude","CAP_FACE",FACE,{"disambiguationData":[OSD([sQuery(id+"F19.wireOp",EDGE,"E17.sketch_text.stroke-8"),sQuery(id+"F19.wireOp",EDGE,"E17.sketch_text.stroke-9"),sQuery(id+"F19.wireOp",EDGE,"E17.sketch_text.stroke-10"),sQuery(id+"F19.wireOp",EDGE,"E17.sketch_text.stroke-11"),sQuery(id+"F19.wireOp",EDGE,"E17.sketch_text.stroke-12"),sQuery(id+"F19.wireOp",EDGE,"E17.sketch_text.stroke-13"),sQuery(id+"F19.wireOp",EDGE,"E17.sketch_text.stroke-14"),sQuery(id+"F19.wireOp",EDGE,"E17.sketch_text.stroke-15"),sQuery(id+"F19.wireOp",EDGE,"E17.sketch_text.stroke-16"),sQuery(id+"F19.wireOp",EDGE,"E17.sketch_text.stroke-17"),sQuery(id+"F19.wireOp",EDGE,"E17.sketch_text.stroke-18"),sQuery(id+"F19.wireOp",EDGE,"E17.sketch_text.stroke-19"),sQuery(id+"F19.wireOp",EDGE,"E17.sketch_text.stroke-20"),sQuery(id+"F19.wireOp",EDGE,"E17.sketch_text.stroke-21"),sQuery(id+"F19.wireOp",EDGE,"E17.sketch_text.stroke-22"),sQuery(id+"F19.wireOp",EDGE,"E17.sketch_text.stroke-23"),sQuery(id+"F19.wireOp",EDGE,"E17.sketch_text.stroke-24"),sQuery(id+"F19.wireOp",EDGE,"E17.sketch_text.stroke-25"),sQuery(id+"F19.wireOp",EDGE,"E17.sketch_text.stroke-26")])],"isStart":false});
            var Q12;
            Q12=makeQuery(id+"F20.opExtrude","CAP_FACE",FACE,{"disambiguationData":[OSD([sQuery(id+"F19.wireOp",EDGE,"E17.sketch_text.stroke-0"),sQuery(id+"F19.wireOp",EDGE,"E17.sketch_text.stroke-1"),sQuery(id+"F19.wireOp",EDGE,"E17.sketch_text.stroke-2"),sQuery(id+"F19.wireOp",EDGE,"E17.sketch_text.stroke-3"),sQuery(id+"F19.wireOp",EDGE,"E17.sketch_text.stroke-4"),sQuery(id+"F19.wireOp",EDGE,"E17.sketch_text.stroke-5"),sQuery(id+"F19.wireOp",EDGE,"E17.sketch_text.stroke-6"),sQuery(id+"F19.wireOp",EDGE,"E17.sketch_text.stroke-7")])],"isStart":false});
            var Q13;
            Q13=makeQuery(id+"F20.opExtrude","CAP_FACE",FACE,{"disambiguationData":[OSD([sQuery(id+"F19.wireOp",EDGE,"E18.sketch_text.stroke-0"),sQuery(id+"F19.wireOp",EDGE,"E18.sketch_text.stroke-1"),sQuery(id+"F19.wireOp",EDGE,"E18.sketch_text.stroke-2"),sQuery(id+"F19.wireOp",EDGE,"E18.sketch_text.stroke-3"),sQuery(id+"F19.wireOp",EDGE,"E18.sketch_text.stroke-4"),sQuery(id+"F19.wireOp",EDGE,"E18.sketch_text.stroke-5"),sQuery(id+"F19.wireOp",EDGE,"E18.sketch_text.stroke-6"),sQuery(id+"F19.wireOp",EDGE,"E18.sketch_text.stroke-7")])],"isStart":false});
            fillet(context, id + "F21", {"entities" : qUnion([Q0, Q1, Q2, Q3, Q4, Q5, Q6, Q7, Q8, Q9, Q10, Q11, Q12, Q13]), "radius" : 0.2 * mm, "tangentPropagation" : true, "allowEdgeOverflow" : false});
        }
        {
            var Q0;
            Q0 = qSketchRegion(id + "F14", true);
            extrude(context, id + "F22", {"entities" : qUnion([Q0]), "operationType" : NewBodyOperationType.REMOVE, "oppositeDirection" : true, "depth" : 2 * mm, "offsetDistance" : 25 * mm});
        }
        {
            var Q0;
            Q0=makeQuery(id+"F22.boolean.opBoolean","SPLIT",FACE,{"disambiguationData":[TD([makeQuery(id+"F22.opExtrude","SWEPT_FACE",FACE,{"disambiguationData":[OSD([sQuery(id+"F14.wireOp",EDGE,"E15.sketch_text.stroke-8")])]})])],"derivedFrom":makeQuery(id+"F7.opExtrude","CAP_FACE",FACE,{"disambiguationData":[OSD([sQuery(id+"F0.wireOp",EDGE,"E5.bottom"),sQuery(id+"F0.wireOp",EDGE,"E5.top"),sQuery(id+"F0.wireOp",EDGE,"E5.left"),sQuery(id+"F0.wireOp",EDGE,"E5.right")])],"isStart":false})});
            var Q1;
            Q1=makeQuery(id+"F22.boolean.opBoolean","COPY",EDGE,{"derivedFrom":makeQuery(id+"F22.opExtrude","CAP_EDGE",EDGE,{"disambiguationData":[OSD([sQuery(id+"F14.wireOp",EDGE,"E15.sketch_text.stroke-7")])],"isStart":true})});
            var Q2;
            Q2=makeQuery(id+"F22.boolean.opBoolean","COPY",EDGE,{"derivedFrom":makeQuery(id+"F22.opExtrude","CAP_EDGE",EDGE,{"disambiguationData":[OSD([sQuery(id+"F14.wireOp",EDGE,"E15.sketch_text.stroke-0")])],"isStart":true})});
            var Q3;
            Q3=makeQuery(id+"F22.boolean.opBoolean","COPY",EDGE,{"derivedFrom":makeQuery(id+"F22.opExtrude","CAP_EDGE",EDGE,{"disambiguationData":[OSD([sQuery(id+"F14.wireOp",EDGE,"E15.sketch_text.stroke-17")])],"isStart":true})});
            var Q4;
            Q4=makeQuery(id+"F22.boolean.opBoolean","COPY",EDGE,{"derivedFrom":makeQuery(id+"F22.opExtrude","CAP_EDGE",EDGE,{"disambiguationData":[OSD([sQuery(id+"F14.wireOp",EDGE,"E15.sketch_text.stroke-21")])],"isStart":true})});
            var Q5;
            Q5=makeQuery(id+"F22.boolean.opBoolean","COPY",EDGE,{"derivedFrom":makeQuery(id+"F22.opExtrude","CAP_EDGE",EDGE,{"disambiguationData":[OSD([sQuery(id+"F14.wireOp",EDGE,"E15.sketch_text.stroke-22")])],"isStart":true})});
            var Q6;
            Q6=makeQuery(id+"F22.boolean.opBoolean","COPY",EDGE,{"derivedFrom":makeQuery(id+"F22.opExtrude","CAP_EDGE",EDGE,{"disambiguationData":[OSD([sQuery(id+"F14.wireOp",EDGE,"E15.sketch_text.stroke-16")])],"isStart":true})});
            var Q7;
            Q7=makeQuery(id+"F22.boolean.opBoolean","COPY",EDGE,{"derivedFrom":makeQuery(id+"F22.opExtrude","CAP_EDGE",EDGE,{"disambiguationData":[OSD([sQuery(id+"F14.wireOp",EDGE,"E15.sketch_text.stroke-19")])],"isStart":true})});
            var Q8;
            Q8=makeQuery(id+"F22.boolean.opBoolean","COPY",EDGE,{"derivedFrom":makeQuery(id+"F22.opExtrude","CAP_EDGE",EDGE,{"disambiguationData":[OSD([sQuery(id+"F14.wireOp",EDGE,"E15.sketch_text.stroke-37")])],"isStart":true})});
            var Q9;
            Q9=makeQuery(id+"F22.boolean.opBoolean","COPY",EDGE,{"derivedFrom":makeQuery(id+"F22.opExtrude","CAP_EDGE",EDGE,{"disambiguationData":[OSD([sQuery(id+"F14.wireOp",EDGE,"E15.sketch_text.stroke-41")])],"isStart":true})});
            var Q10;
            Q10=makeQuery(id+"F22.boolean.opBoolean","COPY",EDGE,{"derivedFrom":makeQuery(id+"F22.opExtrude","CAP_EDGE",EDGE,{"disambiguationData":[OSD([sQuery(id+"F14.wireOp",EDGE,"E15.sketch_text.stroke-42")])],"isStart":true})});
            var Q11;
            Q11=makeQuery(id+"F22.boolean.opBoolean","COPY",EDGE,{"derivedFrom":makeQuery(id+"F22.opExtrude","CAP_EDGE",EDGE,{"disambiguationData":[OSD([sQuery(id+"F14.wireOp",EDGE,"E15.sketch_text.stroke-23")])],"isStart":true})});
            var Q12;
            Q12=makeQuery(id+"F22.boolean.opBoolean","COPY",EDGE,{"derivedFrom":makeQuery(id+"F22.opExtrude","CAP_EDGE",EDGE,{"disambiguationData":[OSD([sQuery(id+"F14.wireOp",EDGE,"E15.sketch_text.stroke-24")])],"isStart":true})});
            var Q13;
            {var subQ0=sQuery(id+"F0.wireOp",EDGE,"E5.right");var subQ1=sQuery(id+"F0.wireOp",EDGE,"E5.left");var subQ2=sQuery(id+"F0.wireOp",EDGE,"E5.top");var subQ3=sQuery(id+"F0.wireOp",EDGE,"E5.bottom");Q13=makeQuery(id+"F22.boolean.opBoolean","SPLIT",FACE,{"disambiguationData":[TD([makeQuery(id+"F15.boolean.opBoolean","COPY",FACE,{"derivedFrom":makeQuery(id+"F15.opExtrude","SWEPT_FACE",FACE,{"disambiguationData":[OSD([sQuery(id+"F14.wireOp",EDGE,"E14")])]})})])],"derivedFrom":makeQuery(id+"F7.opExtrude","CAP_FACE",FACE,{"disambiguationData":[OSD([subQ3,subQ2,subQ1,subQ0])],"isStart":false})});}
            fillet(context, id + "F23", {"entities" : qUnion([Q0, Q1, Q2, Q3, Q4, Q5, Q6, Q7, Q8, Q9, Q10, Q11, Q12, Q13]), "radius" : 0.3 * mm, "tangentPropagation" : true, "allowEdgeOverflow" : false});
        }
    });
